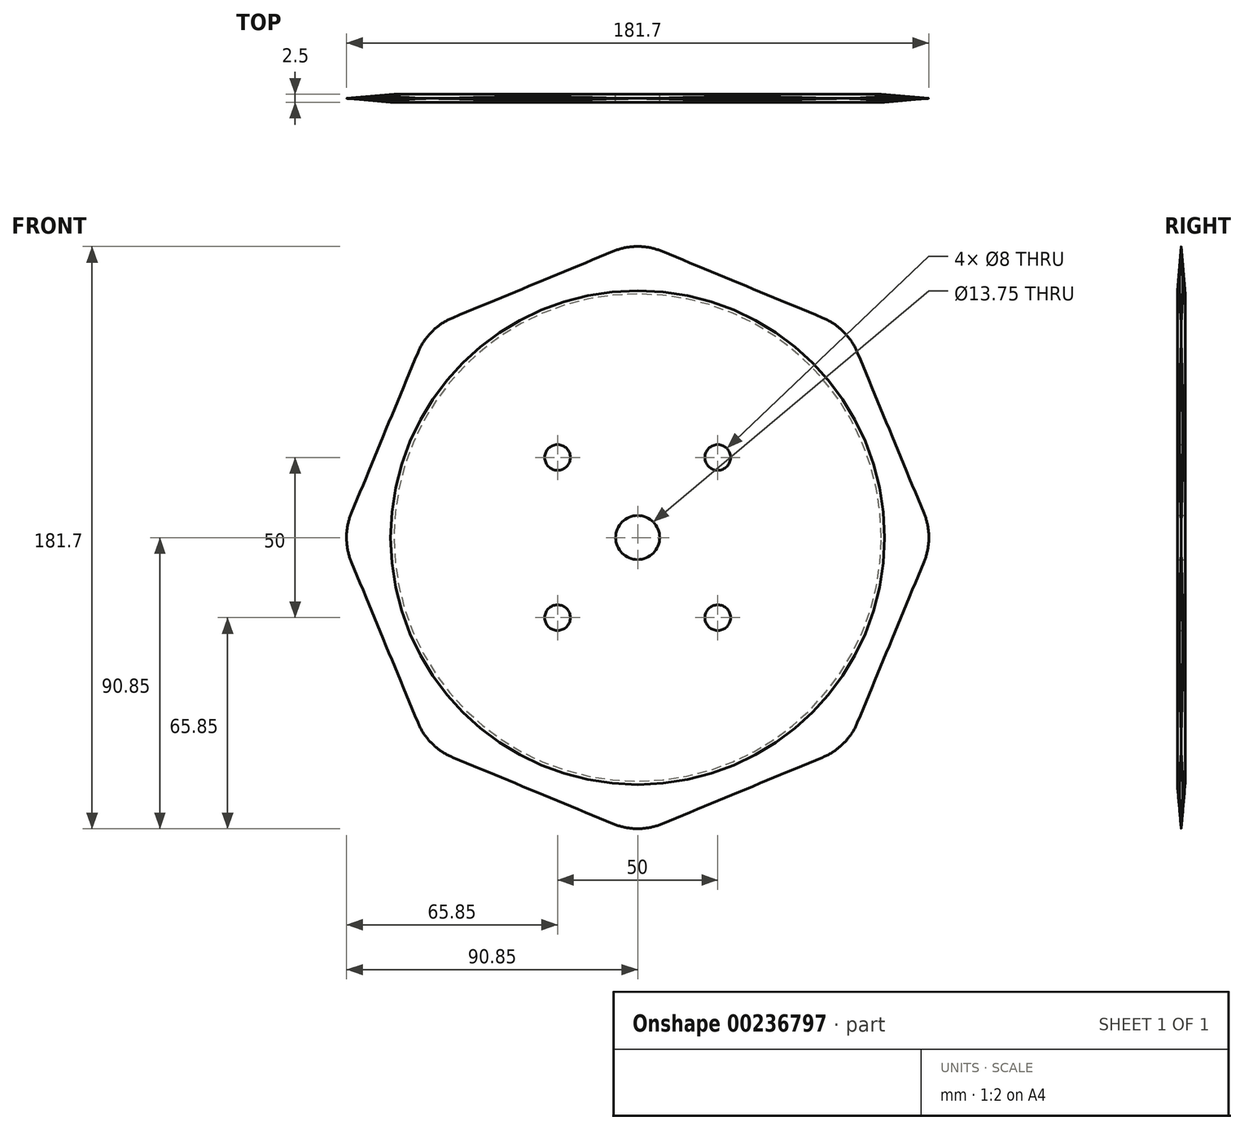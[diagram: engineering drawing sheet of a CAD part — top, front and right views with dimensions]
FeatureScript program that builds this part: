
annotation { "Feature Type Name" : "Feature", "Feature Type Description" : "" }
export const myFeature = defineFeature(function(context is Context, id is Id, definition is map)
    precondition{}
    {
        {
            var Q0;
            Q0=qCreatedBy(makeId("Front.planeOp"),FACE);
            var sketch = newSketch(context, id + "F0", { "sketchPlane" : qUnion([Q0])});
            skCircle(sketch, "E0.cCircle", {"center": v(0, 0) * mm, "radius": 85.46 * mm, "construction": true});
            skLineSegment(sketch, "E0.0", {"start": v(0, 92.5) * mm, "end": v(65.4, 65.4) * mm});
            skLineSegment(sketch, "E0.1", {"start": v(65.4, 65.4) * mm, "end": v(92.5, 0) * mm});
            skLineSegment(sketch, "E0.2", {"start": v(92.5, 0) * mm, "end": v(65.4, -65.4) * mm});
            skLineSegment(sketch, "E0.3", {"start": v(65.4, -65.4) * mm, "end": v(0, -92.5) * mm});
            skLineSegment(sketch, "E0.4", {"start": v(0, -92.5) * mm, "end": v(-65.4, -65.4) * mm});
            skLineSegment(sketch, "E0.5", {"start": v(-65.4, -65.4) * mm, "end": v(-92.5, 0) * mm});
            skLineSegment(sketch, "E0.6", {"start": v(-92.5, 0) * mm, "end": v(-65.4, 65.4) * mm});
            skLineSegment(sketch, "E0.7", {"start": v(-65.4, 65.4) * mm, "end": v(0, 92.5) * mm});
            skPoint(sketch, "E0.0.midPoint", {"position": v(32.7, 78.95) * mm});
            skCircle(sketch, "E1", {"center": v(0, 0) * mm, "radius": 6.88 * mm});
            skLineSegment(sketch, "E2", {"start": v(0, 114.98) * mm, "end": v(0, -127.7) * mm, "construction": true});
            skSolve(sketch);
        }
        {
            var Q0;
            Q0 = qSketchRegion(id + "F0", true);
            var Q1;
            Q1=makeQuery(id+"F0.imprint","IMPRINT",FACE,{"disambiguationData":[TD([[makeQuery(id+"F0.imprint","IMPRINT",EDGE,{"derivedFrom":sQuery(id+"F0.wireOp",EDGE,"E0.0")}),-1.0]])]});
            extrude(context, id + "F1", {"entities" : qUnion([Q0, Q1]), "depth" : 2.5 * mm, "offsetDistance" : 25 * mm});
        }
        {
            var Q0;
            Q0=makeQuery(id+"F1.opExtrude","SWEPT_EDGE",EDGE,{"disambiguationData":[OSD([sQuery(id+"F0.wireOp",EDGE,"E0.5"),sQuery(id+"F0.wireOp",EDGE,"E0.6")])]});
            var Q1;
            Q1=makeQuery(id+"F1.opExtrude","SWEPT_EDGE",EDGE,{"disambiguationData":[OSD([sQuery(id+"F0.wireOp",EDGE,"E0.6"),sQuery(id+"F0.wireOp",EDGE,"E0.7")])]});
            var Q2;
            Q2=makeQuery(id+"F1.opExtrude","SWEPT_EDGE",EDGE,{"disambiguationData":[OSD([sQuery(id+"F0.wireOp",EDGE,"E0.0"),sQuery(id+"F0.wireOp",EDGE,"E0.7")])]});
            var Q3;
            Q3=makeQuery(id+"F1.opExtrude","SWEPT_EDGE",EDGE,{"disambiguationData":[OSD([sQuery(id+"F0.wireOp",EDGE,"E0.0"),sQuery(id+"F0.wireOp",EDGE,"E0.1")])]});
            var Q4;
            Q4=makeQuery(id+"F1.opExtrude","SWEPT_EDGE",EDGE,{"disambiguationData":[OSD([sQuery(id+"F0.wireOp",EDGE,"E0.1"),sQuery(id+"F0.wireOp",EDGE,"E0.2")])]});
            var Q5;
            Q5=makeQuery(id+"F1.opExtrude","SWEPT_EDGE",EDGE,{"disambiguationData":[OSD([sQuery(id+"F0.wireOp",EDGE,"E0.2"),sQuery(id+"F0.wireOp",EDGE,"E0.3")])]});
            var Q6;
            Q6=makeQuery(id+"F1.opExtrude","SWEPT_EDGE",EDGE,{"disambiguationData":[OSD([sQuery(id+"F0.wireOp",EDGE,"E0.3"),sQuery(id+"F0.wireOp",EDGE,"E0.4")])]});
            var Q7;
            Q7=makeQuery(id+"F1.opExtrude","SWEPT_EDGE",EDGE,{"disambiguationData":[OSD([sQuery(id+"F0.wireOp",EDGE,"E0.4"),sQuery(id+"F0.wireOp",EDGE,"E0.5")])]});
            fillet(context, id + "F2", {"entities" : qUnion([Q0, Q1, Q2, Q3, Q4, Q5, Q6, Q7]), "radius" : 20 * mm, "tangentPropagation" : true, "allowEdgeOverflow" : false});
        }
        {
            var Q0;
            Q0=makeQuery(id+"F1.opExtrude","CAP_FACE",FACE,{"disambiguationData":[OSD([sQuery(id+"F0.wireOp",EDGE,"E0.0"),sQuery(id+"F0.wireOp",EDGE,"E0.1"),sQuery(id+"F0.wireOp",EDGE,"E0.2"),sQuery(id+"F0.wireOp",EDGE,"E0.3"),sQuery(id+"F0.wireOp",EDGE,"E0.4"),sQuery(id+"F0.wireOp",EDGE,"E0.5"),sQuery(id+"F0.wireOp",EDGE,"E0.6"),sQuery(id+"F0.wireOp",EDGE,"E0.7"),sQuery(id+"F0.wireOp",EDGE,"E1")])],"isStart":false});
            var sketch = newSketch(context, id + "F3", { "sketchPlane" : qUnion([Q0])});
            skCircle(sketch, "E3", {"center": v(0, 0) * mm, "radius": 35.36 * mm, "construction": true});
            skPoint(sketch, "E4", {"position": v(-25, 25) * mm});
            skPoint(sketch, "E5", {"position": v(25, 25) * mm});
            skPoint(sketch, "E6", {"position": v(25, -25) * mm});
            skPoint(sketch, "E7", {"position": v(-25, -25) * mm});
            skSolve(sketch);
        }
        {
            var Q0;
            Q0=sQuery(id+"F3.wireOp",VERTEX,"E4");
            var Q1;
            Q1=sQuery(id+"F3.wireOp",VERTEX,"E5");
            var Q2;
            Q2=sQuery(id+"F3.wireOp",VERTEX,"E6");
            var Q3;
            Q3=sQuery(id+"F3.wireOp",VERTEX,"E7");
            var Q4;
            Q4=makeQuery(id+"F1.opExtrude","SWEPT_BODY",BODY,{"disambiguationData":[OSD([sQuery(id+"F0.wireOp",EDGE,"E0.0"),sQuery(id+"F0.wireOp",EDGE,"E0.1"),sQuery(id+"F0.wireOp",EDGE,"E0.2"),sQuery(id+"F0.wireOp",EDGE,"E0.3"),sQuery(id+"F0.wireOp",EDGE,"E0.4"),sQuery(id+"F0.wireOp",EDGE,"E0.5"),sQuery(id+"F0.wireOp",EDGE,"E0.6"),sQuery(id+"F0.wireOp",EDGE,"E0.7"),sQuery(id+"F0.wireOp",EDGE,"E1")])]});
            hole(context, id + "F4", {"style" : HoleStyle.SIMPLE, "endStyle" : HoleEndStyle.THROUGH, "standardTappedOrClearance" : lookupTablePath({ "fit" : "Standard", "standard" : "ISO", "size" : "M12", "type" : "Clearance" }), "standardBlindInLast" : lookupTablePath({ "fit" : "Standard", "standard" : "ISO", "size" : "M12", "type" : "Clearance" }), "holeDiameter" : 8 * mm, "majorDiameter" : 5 * mm, "isTappedThrough" : true, "tappedDepth" : 28 * mm, "tapClearance" : 3, "locations" : qUnion([Q0, Q1, Q2, Q3]), "scope" : qUnion([Q4])});
        }
        {
            var Q0;
            Q0=qCreatedBy(makeId("Top.planeOp"),FACE);
            var sketch = newSketch(context, id + "F5", { "sketchPlane" : qUnion([Q0])});
            skLineSegment(sketch, "E8", {"start": v(0, -35.5) * mm, "end": v(0, 37.14) * mm, "construction": true});
            skLineSegment(sketch, "E9", {"start": v(90.85, -1.3) * mm, "end": v(45.13, -5.3) * mm});
            skLineSegment(sketch, "E10", {"start": v(45.13, -5.3) * mm, "end": v(94.06, -5.3) * mm});
            skLineSegment(sketch, "E11", {"start": v(94.06, -5.3) * mm, "end": v(94.06, 2.7) * mm});
            skLineSegment(sketch, "E12", {"start": v(94.06, 2.7) * mm, "end": v(45.13, 2.7) * mm});
            skLineSegment(sketch, "E13", {"start": v(45.13, 2.7) * mm, "end": v(90.85, -1.3) * mm});
            skSolve(sketch);
        }
        {
            var Q0;
            Q0 = qSketchRegion(id + "F5", true);
            var Q1;
            Q1=sQuery(id+"F5.wireOp",EDGE,"E8");
            revolve(context, id + "F6", {"operationType" : NewBodyOperationType.REMOVE, "surfaceOperationType" : NewSurfaceOperationType.NEW, "entities" : qUnion([Q0]), "axis" : qUnion([Q1]), "revolveType" : RevolveType.FULL, "oppositeDirection" : true});
        }
    });
